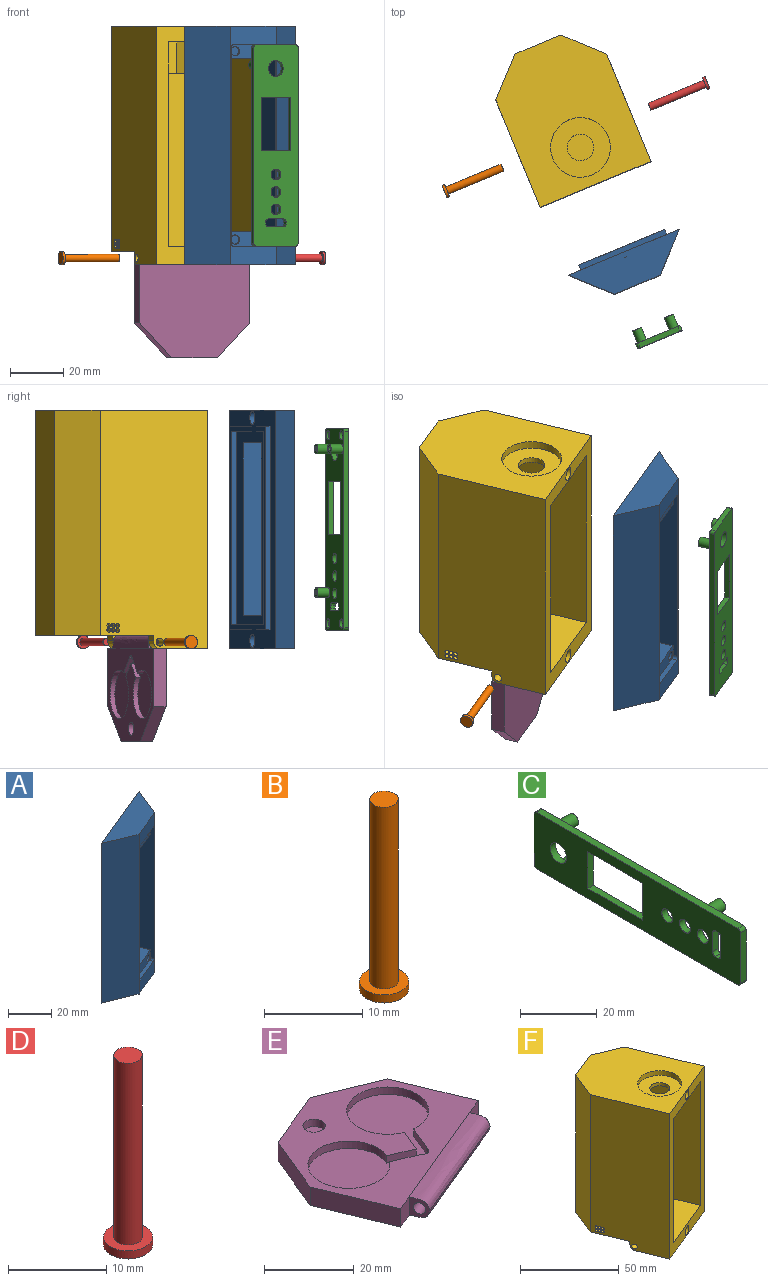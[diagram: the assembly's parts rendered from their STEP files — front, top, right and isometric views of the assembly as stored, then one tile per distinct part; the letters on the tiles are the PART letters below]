
ASSEMBLY  parts=6 mates=5
PART A: 40 faces, bbox 41.8x24.5x90 mm
  f0: plane 90x17.32mm, normal (0.38,-0.92,0), area 320.4mm2, adj f2,f3,f4,f5,f20,f22,f24,f25
  f1: plane 90x41.82mm, normal (-0.38,0.92,0), area 1341.6mm2, adj f2,f3,f4,f5,f6,f7,f8,f13
  f2: plane 41.82x24.5mm, normal (0,0,-1), area 424.4mm2, adj f0,f1,f3,f4
  f3: plane 90x17.32mm, normal (-0.38,-0.92,0), area 1687.5mm2, adj f0,f1,f2,f5
  f4: plane 90x17.32mm, normal (0.92,-0.38,0), area 1687.5mm2, adj f0,f1,f2,f5
  f5: plane 41.82x24.5mm, normal (0,0,1), area 424.4mm2, adj f0,f1,f3,f4
  f6: plane 76.8x1.85mm, normal (0.92,0.38,0), area 153.6mm2, adj f1,f7,f13,f14
  f7: plane 33.16x15.27mm, normal (0,0,-1), area 70.1mm2, adj f1,f6,f8,f14
  f8: plane 76.8x1.85mm, normal (-0.92,-0.38,0), area 153.6mm2, adj f1,f7,f13,f14
  f9: plane 29.47x13.74mm, normal (0,0,1), area 62.1mm2, adj f10,f12,f14,f15
  f10: plane 72.8x1.85mm, normal (-0.92,-0.38,0), area 145.6mm2, adj f9,f11,f14,f15
  f11: plane 29.47x13.74mm, normal (0,0,-1), area 62.1mm2, adj f10,f12,f14,f15
  f12: plane 72.8x1.85mm, normal (0.92,0.38,0), area 145.6mm2, adj f9,f11,f14,f15
  f13: plane 33.16x15.27mm, normal (0,0,1), area 70.1mm2, adj f1,f6,f8,f14
  f14: plane 76.8x32.4mm, normal (-0.38,0.92,0), area 431.5mm2, adj f6,f7,f8,f9,f10,f11,f12,f13
  f15: plane 72.8x28.7mm, normal (-0.38,0.92,0), area 1087.5mm2, adj f9,f10,f11,f12,f20,f21,f22,f23
  f16: cylinder r=2.5mm len=5.38mm, axis (-0.38,0.92,0), area 31.4mm2, adj f1,f17
  f17: plane 5x4.62mm, normal (-0.38,0.92,0), area 19.6mm2, adj f16
  f18: cylinder r=2.5mm len=5.38mm, axis (-0.38,0.92,0), area 31.4mm2, adj f1,f19
  f19: plane 5x4.62mm, normal (-0.38,0.92,0), area 19.6mm2, adj f18
  f20: plane 74x12.25mm, normal (0.92,0.38,0), area 882.4mm2, adj f0,f15,f21,f23,f24,f27,f30,f31
  f21: plane 20.94x17.29mm, normal (0,0,1), area 202.6mm2, adj f15,f20,f22,f27
  f22: plane 74x12.25mm, normal (-0.92,-0.38,0), area 882.4mm2, adj f0,f15,f21,f23,f26,f27,f28,f31
  f23: plane 20.94x17.29mm, normal (0,0,-1), area 202.6mm2, adj f15,f20,f22,f31
  f24: cylinder r=1mm len=2.23mm, axis (0.38,-0.92,0), area 3.1mm2, adj f0,f20,f25,f27
  f25: plane 15.55x7.97mm, normal (0,0,1), area 32mm2, adj f0,f24,f26,f27
  f26: cylinder r=1mm len=2.23mm, axis (0.38,-0.92,0), area 3.1mm2, adj f0,f22,f25,f27
  f27: plane 16.63x6.89mm, normal (0.38,-0.92,0), area 77.3mm2, adj f20,f21,f22,f24,f25,f26,f36,f38
  f28: cylinder r=1mm len=2.23mm, axis (0.38,-0.92,0), area 3.1mm2, adj f0,f22,f29,f31
  f29: plane 15.55x7.97mm, normal (0,0,-1), area 32mm2, adj f0,f28,f30,f31
  f30: cylinder r=1mm len=2.23mm, axis (0.38,-0.92,0), area 3.1mm2, adj f0,f20,f29,f31
  f31: plane 16.63x6.89mm, normal (0.38,-0.92,0), area 77.3mm2, adj f20,f22,f23,f28,f29,f30,f32,f34
  f32: cylinder r=1.75mm len=3.62mm, axis (0.38,-0.92,0), area 11mm2, adj f31,f33
  f33: plane 3.5x3.23mm, normal (0.38,-0.92,0), area 9.6mm2, adj f32
  f34: cylinder r=1.75mm len=3.62mm, axis (0.38,-0.92,0), area 11mm2, adj f31,f35
  f35: plane 3.5x3.23mm, normal (0.38,-0.92,0), area 9.6mm2, adj f34
  f36: cylinder r=1.75mm len=3.62mm, axis (0.38,-0.92,0), area 11mm2, adj f27,f37
  f37: plane 3.5x3.23mm, normal (0.38,-0.92,0), area 9.6mm2, adj f36
  f38: cylinder r=1.75mm len=3.62mm, axis (0.38,-0.92,0), area 11mm2, adj f27,f39
  f39: plane 3.5x3.23mm, normal (0.38,-0.92,0), area 9.6mm2, adj f38
PART B: 5 faces, bbox 5x5x23.6 mm
  f0: cylinder r=2.5mm len=5mm, axis (0,0,-1), area 15.7mm2, adj f1,f2
  f1: plane 5x5mm, normal (0,0,1), area 13mm2, adj f0,f3
  f2: plane 5x5mm, normal (0,0,-1), area 19.6mm2, adj f0
  f3: cylinder r=1.45mm len=22.63mm, axis (0,0,-1), area 206.2mm2, adj f1,f4
  f4: plane 2.9x2.9mm, normal (0,0,1), area 6.6mm2, adj f3
PART C: 46 faces, bbox 6.9x76x18 mm
  f0: plane 74x2mm, normal (0,0,-1), area 148mm2, adj f18,f19,f43,f44
  f1: plane 74x2mm, normal (0,0,1), area 148mm2, adj f18,f19,f42,f45
  f2: cylinder r=1mm len=2mm, axis (-1,0,0), area 3.1mm2, adj f3,f12,f18,f19
  f3: plane 2x1mm, normal (0,0,1), area 2mm2, adj f2,f4,f18,f19
  f4: cylinder r=1mm len=2mm, axis (-1,0,0), area 3.1mm2, adj f3,f5,f18,f19
  f5: plane 6.2x2mm, normal (0,1,0), area 12.4mm2, adj f4,f6,f18,f19
  f6: cylinder r=1mm len=2mm, axis (-1,0,0), area 3.1mm2, adj f5,f7,f18,f19
  f7: plane 2x1mm, normal (0,0,-1), area 2mm2, adj f6,f8,f18,f19
  f8: cylinder r=1mm len=2mm, axis (-1,0,0), area 3.1mm2, adj f7,f12,f18,f19
  f9: plane 11.72x2mm, normal (0,1,0), area 23.4mm2, adj f10,f13,f18,f19
  f10: plane 20.16x2mm, normal (0,0,-1), area 40.3mm2, adj f9,f11,f18,f19
  f11: plane 11.72x2mm, normal (0,-1,0), area 23.4mm2, adj f10,f13,f18,f19
  f12: plane 6.2x2mm, normal (0,-1,0), area 12.4mm2, adj f2,f8,f18,f19
  f13: plane 20.16x2mm, normal (0,0,1), area 40.3mm2, adj f9,f11,f18,f19
  f14: cylinder r=2mm len=4mm, axis (-1,0,0), area 25.1mm2, adj f18,f19
  f15: cylinder r=2mm len=4mm, axis (-1,0,0), area 25.1mm2, adj f18,f19
  f16: cylinder r=2mm len=4mm, axis (-1,0,0), area 25.1mm2, adj f18,f19
  f17: cylinder r=3mm len=6mm, axis (-1,0,0), area 37.7mm2, adj f18,f19
  f18: plane 76x18mm, normal (1,0,0), area 972.1mm2, adj f0,f1,f2,f3,f4,f5,f6,f7
  f19: plane 76x18mm, normal (-1,0,0), area 1041.2mm2, adj f0,f1,f2,f3,f4,f5,f6,f7
  f20: cylinder r=1.8mm len=4.9mm, axis (-1,0,0), area 55.4mm2, adj f18,f22
  f21: cylinder r=0.8mm len=5.9mm, axis (-1,0,0), area 29.7mm2, adj f22,f30
  f22: plane 3.6x3.6mm, normal (1,0,0), area 8.2mm2, adj f20,f21
  f23: cylinder r=1.8mm len=4.9mm, axis (-1,0,0), area 55.4mm2, adj f18,f25
  f24: cylinder r=0.8mm len=5.9mm, axis (-1,0,0), area 29.7mm2, adj f25,f31
  f25: plane 3.6x3.6mm, normal (1,0,0), area 8.2mm2, adj f23,f24
  f26: cylinder r=1.8mm len=4.9mm, axis (-1,0,0), area 55.4mm2, adj f18,f28
  f27: cylinder r=0.8mm len=5.9mm, axis (-1,0,0), area 29.7mm2, adj f28,f29
  f28: plane 3.6x3.6mm, normal (1,0,0), area 8.2mm2, adj f26,f27
  f29: plane 1.6x1.6mm, normal (1,0,0), area 2mm2, adj f27
  f30: plane 1.6x1.6mm, normal (1,0,0), area 2mm2, adj f21
  f31: plane 1.6x1.6mm, normal (1,0,0), area 2mm2, adj f24
  f32: plane 16x2mm, normal (0,-1,0), area 32mm2, adj f18,f19,f44,f45
  f33: plane 16x2mm, normal (0,1,0), area 32mm2, adj f18,f19,f42,f43
  f34: cylinder r=1.75mm len=3.5mm, axis (1,0,0), area 11mm2, adj f18,f35
  f35: plane 3.5x3.5mm, normal (1,0,0), area 9.6mm2, adj f34
  f36: cylinder r=1.75mm len=3.5mm, axis (1,0,0), area 11mm2, adj f18,f37
  f37: plane 3.5x3.5mm, normal (1,0,0), area 9.6mm2, adj f36
  f38: cylinder r=1.75mm len=3.5mm, axis (1,0,0), area 11mm2, adj f18,f39
  f39: plane 3.5x3.5mm, normal (1,0,0), area 9.6mm2, adj f38
  f40: cylinder r=1.75mm len=3.5mm, axis (1,0,0), area 11mm2, adj f18,f41
  f41: plane 3.5x3.5mm, normal (1,0,0), area 9.6mm2, adj f40
  f42: cylinder r=1mm len=2mm, axis (-1,0,0), area 3.1mm2, adj f1,f18,f19,f33
  f43: cylinder r=1mm len=2mm, axis (1,0,0), area 3.1mm2, adj f0,f18,f19,f33
  f44: cylinder r=1mm len=2mm, axis (-1,0,0), area 3.1mm2, adj f0,f18,f19,f32
  f45: cylinder r=1mm len=2mm, axis (1,0,0), area 3.1mm2, adj f1,f18,f19,f32
PART D: 5 faces, bbox 5x5x23.6 mm
  f0: cylinder r=2.5mm len=5mm, axis (0,0,-1), area 15.7mm2, adj f1,f2
  f1: plane 5x5mm, normal (0,0,1), area 13mm2, adj f0,f3
  f2: plane 5x5mm, normal (0,0,-1), area 19.6mm2, adj f0
  f3: cylinder r=1.45mm len=22.63mm, axis (0,0,-1), area 206.2mm2, adj f1,f4
  f4: plane 2.9x2.9mm, normal (0,0,1), area 6.6mm2, adj f3
PART E: 24 faces, bbox 50.9x48.8x5.7 mm
  f0: plane 5x4.62mm, normal (0.38,-0.92,0), area 25mm2, adj f4,f6,f16,f19
  f1: plane 5x4.62mm, normal (0.38,-0.92,0), area 25mm2, adj f4,f7,f16,f20
  f2: cylinder r=9.15mm len=18.3mm, axis (0,0,-1), area 110.1mm2, adj f4,f11,f13,f14
  f3: cylinder r=9.15mm len=18.3mm, axis (0,0,-1), area 110.1mm2, adj f4,f11,f12,f15
  f4: plane 50.19x44.71mm, normal (0,0,1), area 828.8mm2, adj f0,f1,f2,f3,f5,f6,f7,f8
  f5: cylinder r=1.5mm len=2.7mm, axis (0,0,1), area 7.5mm2, adj f4,f11,f14,f15
  f6: plane 20.21x8.37mm, normal (0.92,0.38,0), area 109.4mm2, adj f0,f4,f10,f16
  f7: plane 20.21x8.37mm, normal (-0.92,-0.38,0), area 109.4mm2, adj f1,f4,f8,f16
  f8: plane 17.32x7.18mm, normal (-0.92,0.38,0), area 93.8mm2, adj f4,f7,f9,f16
  f9: plane 17.32x7.18mm, normal (-0.38,0.92,0), area 93.8mm2, adj f4,f8,f10,f16
  f10: plane 17.32x7.18mm, normal (0.38,0.92,0), area 93.8mm2, adj f4,f6,f9,f16
  f11: plane 39.21x27.02mm, normal (0,0,1), area 566.2mm2, adj f2,f3,f5,f12,f13,f14,f15
  f12: plane 6.41x2.71mm, normal (0.92,-0.39,0), area 13.9mm2, adj f3,f4,f11,f13
  f13: plane 6.5x2.75mm, normal (-0.39,-0.92,0), area 14.1mm2, adj f2,f4,f11,f12
  f14: plane 7.04x2.98mm, normal (0.39,0.92,0), area 15.3mm2, adj f2,f4,f5,f11
  f15: plane 7.26x3.07mm, normal (-0.92,0.39,0), area 15.8mm2, adj f3,f4,f5,f11
  f16: plane 50.19x44.71mm, normal (0,0,-1), area 1414.6mm2, adj f0,f1,f6,f7,f8,f9,f10,f22
  f17: cylinder r=2.5mm len=5mm, axis (0,0,1), area 31.4mm2, adj f4,f18
  f18: plane 5x5mm, normal (0,0,1), area 19.6mm2, adj f17
  f19: plane 5.73x5.35mm, normal (0.92,0.38,0), area 14.6mm2, adj f0,f21,f22,f23
  f20: plane 5.73x5.35mm, normal (-0.92,-0.38,0), area 14.6mm2, adj f1,f21,f22,f23
  f21: cylinder r=1.5mm len=33.73mm, axis (0.92,0.38,0), area 332.4mm2, adj f19,f20
  f22: bspline ~37.75x19.47mm, area 223.2mm2, adj f16,f19,f20,f23
  f23: bspline ~37.75x19.47mm, area 223.2mm2, adj f4,f19,f20,f22
PART F: 58 faces, bbox 58.6x64.9x90 mm
  f0: plane 4.62x2mm, normal (-0.38,0.92,0), area 10mm2, adj f1,f31,f39,f45
  f1: plane 90x40.42mm, normal (-0.92,-0.38,0), area 3809mm2, adj f0,f11,f12,f14,f23,f31,f43,f45
  f2: cylinder r=9.15mm len=60mm, axis (0,0,-1), area 3438.9mm2, adj f16,f31,f46,f47,f48,f49,f50,f51
  f3: cylinder r=9.15mm len=60mm, axis (0,0,-1), area 3438.8mm2, adj f15,f31,f52,f53,f54,f55,f56,f57
  f4: plane 77x38.51mm, normal (0.92,0.38,0), area 2385.1mm2, adj f7,f14,f21,f26,f27,f29
  f5: cylinder r=10mm len=20mm, axis (0,0,-1), area 52mm2, adj f6,f27,f28
  f6: extruded ~11.69x10.94mm, area 25.8mm2, adj f5,f27,f28
  f7: plane 65x32.58mm, normal (0.38,-0.92,0), area 2292.3mm2, adj f4,f20,f26,f29
  f8: cylinder r=5mm len=10mm, axis (0,0,1), area 62.8mm2, adj f25,f28
  f9: plane 85x17.32mm, normal (0.38,0.92,0), area 1593.8mm2, adj f10,f13,f23,f31
  f10: plane 85x17.32mm, normal (-0.38,0.92,0), area 1593.8mm2, adj f9,f11,f23,f31
  f11: plane 85x17.32mm, normal (-0.92,0.38,0), area 1593.8mm2, adj f1,f10,f23,f31
  f12: plane 49.04x34.76mm, normal (0,0,-1), area 783.9mm2, adj f1,f13,f14,f39,f40,f41,f44,f45
  f13: plane 90x40.42mm, normal (0.92,0.38,0), area 3809mm2, adj f9,f12,f14,f23,f30,f31,f42,f44
  f14: plane 90x41.82mm, normal (0.38,-0.92,0), area 1319.2mm2, adj f1,f4,f12,f13,f20,f23,f26,f27
  f15: plane 18.3x18.3mm, normal (0,0,-1), area 242.6mm2, adj f3,f18
  f16: plane 18.3x18.3mm, normal (0,0,-1), area 242.6mm2, adj f2,f17
  f17: cylinder r=2.55mm len=7mm, axis (0,0,-1), area 112.2mm2, adj f16,f29
  f18: cylinder r=2.55mm len=7mm, axis (0,0,-1), area 112.2mm2, adj f15,f29
  f19: plane 13.5x12mm, normal (-0.38,-0.92,0), area 175.3mm2, adj f20,f22,f27,f29
  f20: plane 77x38.51mm, normal (-0.92,-0.38,0), area 2385.1mm2, adj f7,f14,f19,f26,f27,f29
  f21: plane 13.5x12mm, normal (0.92,-0.38,0), area 175.3mm2, adj f4,f22,f27,f29
  f22: plane 13.5x12mm, normal (0.38,-0.92,0), area 175.3mm2, adj f19,f21,f27,f29
  f23: plane 64.92x58.56mm, normal (0,0,1), area 2007.2mm2, adj f1,f9,f10,f11,f13,f14,f24
  f24: cylinder r=11.25mm len=22.5mm, axis (0,0,1), area 212.1mm2, adj f23,f25
  f25: plane 22.5x22.5mm, normal (0,0,1), area 319.1mm2, adj f8,f24
  f26: plane 43.68x40.29mm, normal (0,0,1), area 1015.7mm2, adj f4,f7,f14,f20,f32
  f27: plane 57.59x48.53mm, normal (0,0,-1), area 1333.9mm2, adj f4,f5,f6,f14,f19,f20,f21,f22
  f28: plane 28.47x20mm, normal (0,0,-1), area 315mm2, adj f5,f6,f8
  f29: plane 37.43x30.8mm, normal (0,0,1), area 663.9mm2, adj f4,f7,f17,f18,f19,f20,f21,f22
  f30: plane 4.62x2mm, normal (-0.38,0.92,0), area 10mm2, adj f13,f31,f40,f44
  f31: plane 50.19x47.41mm, normal (0,0,-1), area 1038.2mm2, adj f0,f1,f2,f3,f9,f10,f11,f13
  f32: cylinder r=1.5mm len=3mm, axis (0,0,-1), area 18.8mm2, adj f26,f31
  f33: cylinder r=2.5mm len=5.38mm, axis (0.38,-0.92,0), area 31.4mm2, adj f14,f34
  f34: plane 5x4.62mm, normal (0.38,-0.92,0), area 19.6mm2, adj f33
  f35: cylinder r=2.5mm len=5.38mm, axis (0.38,-0.92,0), area 31.4mm2, adj f14,f36
  f36: plane 5x4.62mm, normal (0.38,-0.92,0), area 19.6mm2, adj f35
  f37: cylinder r=2.5mm len=5mm, axis (0,0,-1), area 31.4mm2, adj f31,f38
  f38: plane 5x5mm, normal (0,0,-1), area 19.6mm2, adj f37
  f39: plane 5x4.62mm, normal (0.92,0.38,0), area 16.4mm2, adj f0,f12,f31,f41,f43,f45
  f40: plane 5x4.62mm, normal (-0.92,-0.38,0), area 16.4mm2, adj f12,f30,f31,f41,f42,f44
  f41: plane 32.58x13.5mm, normal (-0.38,0.92,0), area 176.3mm2, adj f12,f31,f39,f40
  f42: cylinder r=1.5mm len=5.77mm, axis (-0.92,-0.38,0), area 47.1mm2, adj f13,f40
  f43: cylinder r=1.5mm len=5.77mm, axis (0.92,0.38,0), area 47.1mm2, adj f1,f39
  f44: bspline ~6.23x4.88mm, area 24.3mm2, adj f12,f13,f30,f40
  f45: bspline ~6.23x4.88mm, area 24.3mm2, adj f0,f1,f12,f39
  f46: cylinder r=0.75mm len=3.1mm, axis (0.92,0.38,0), area 11.8mm2, adj f2,f13
  f47: cylinder r=0.75mm len=2.77mm, axis (0.92,0.38,0), area 10.6mm2, adj f2,f13
  f48: cylinder r=0.75mm len=3.1mm, axis (0.92,0.38,0), area 11.8mm2, adj f2,f13
  f49: cylinder r=0.75mm len=2.67mm, axis (0.92,0.38,0), area 10.4mm2, adj f2,f13
  f50: cylinder r=0.75mm len=2.67mm, axis (0.92,0.38,0), area 10.4mm2, adj f2,f13
  f51: cylinder r=0.75mm len=2.77mm, axis (0.92,0.38,0), area 10.6mm2, adj f2,f13
  f52: cylinder r=0.75mm len=2.77mm, axis (-0.92,-0.38,0), area 10.6mm2, adj f1,f3
  f53: cylinder r=0.75mm len=2.77mm, axis (-0.92,-0.38,0), area 10.6mm2, adj f1,f3
  f54: cylinder r=0.75mm len=3.1mm, axis (-0.92,-0.38,0), area 11.8mm2, adj f1,f3
  f55: cylinder r=0.75mm len=2.67mm, axis (-0.92,-0.38,0), area 10.4mm2, adj f1,f3
  f56: cylinder r=0.75mm len=2.67mm, axis (-0.92,-0.38,0), area 10.4mm2, adj f1,f3
  f57: cylinder r=0.75mm len=3.1mm, axis (-0.92,-0.38,0), area 11.8mm2, adj f1,f3
PLACE A t=(-141.54,56.93,-17.32)mm
PLACE B rot(axis=(-0.7,-0.14,-0.7),164.1deg) t=(-180.82,19.15,-42.85)mm
PLACE C rot(axis=(0.43,0.64,0.64),133.7deg) t=(-99.29,-36.63,20.56)mm
PLACE D rot(axis=(0.7,0.14,-0.7),164.1deg) t=(-81.72,60.2,4.53)mm
PLACE E rot(axis=(-0.92,-0.38,0),90deg) t=(-139.88,60.46,-29.82)mm
PLACE F t=(-137.01,53.53,-17.32)mm
MATE slider C.f18 <-> A.f31  axis (-0.38,0.92,0) through (-100.38,-34.91,65.68)mm
MATE slider B.f0 <-> F.f42  axis (0.92,0.38,0) through (-179.9,19.53,-14.82)mm
MATE slider D.f0 <-> F.f42  axis (-0.92,-0.38,0) through (-82.65,59.82,-14.82)mm
MATE revolute E.f21 <-> F.f42  axis (0.92,0.38,0) through (-114.98,46.42,-14.82)mm
MATE slider A.f1 <-> F.f14  axis (-0.38,0.92,0) through (-113.25,-3.83,72.68)mm
